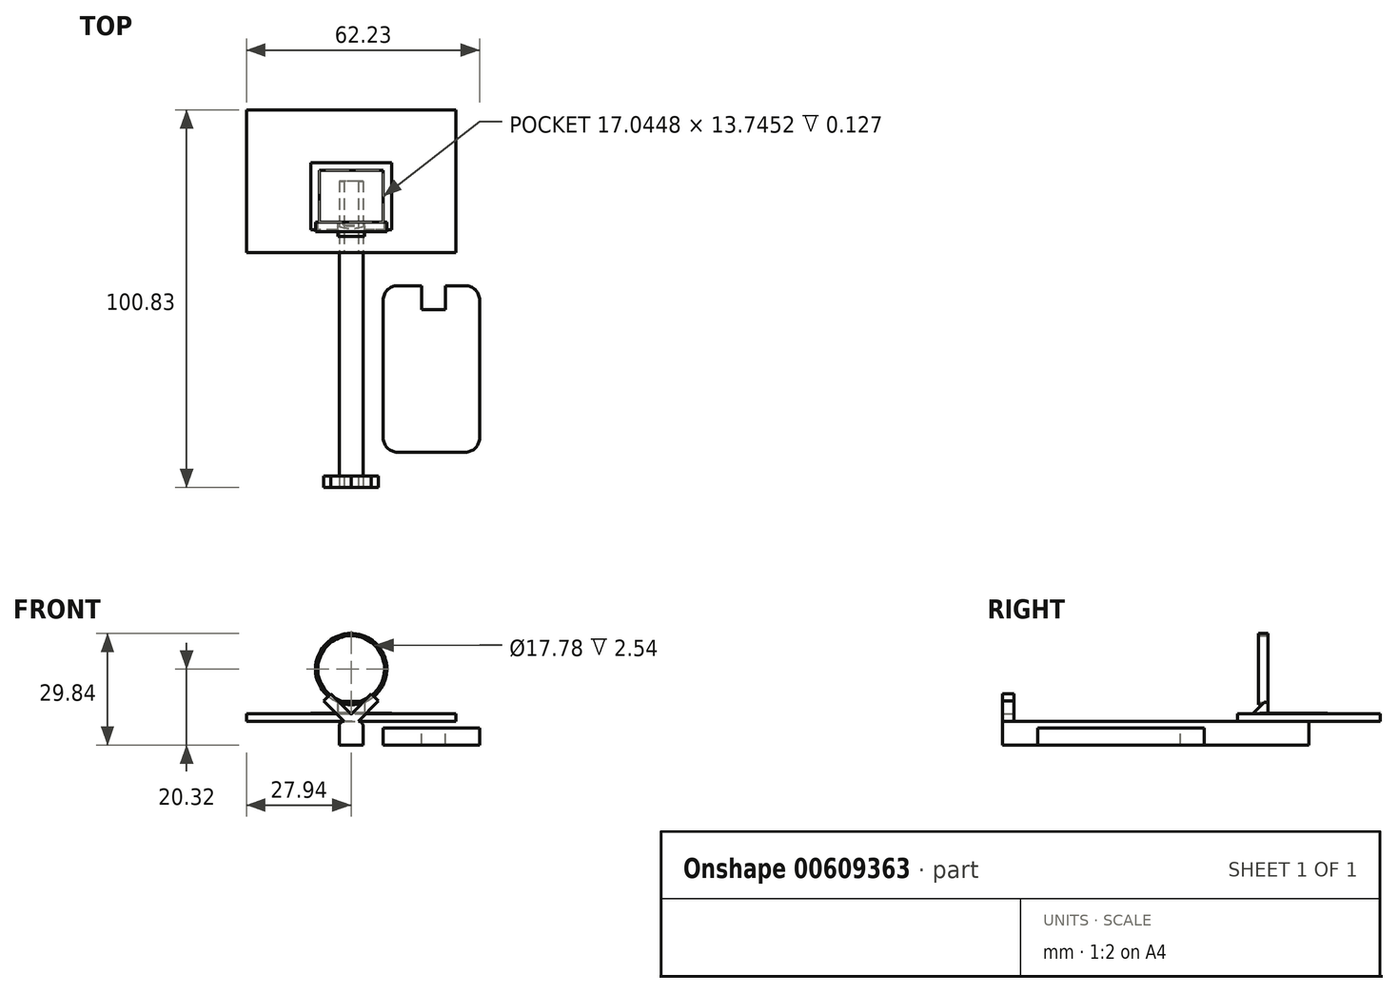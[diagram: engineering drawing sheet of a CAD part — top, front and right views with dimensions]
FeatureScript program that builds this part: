
annotation { "Feature Type Name" : "Feature", "Feature Type Description" : "" }
export const myFeature = defineFeature(function(context is Context, id is Id, definition is map)
    precondition{}
    {
        {
            var Q0;
            Q0=qCreatedBy(makeId("Top.planeOp"),FACE);
            var sketch = newSketch(context, id + "F0", { "sketchPlane" : qUnion([Q0])});
            skLineSegment(sketch, "E0.bottom", {"start": v(3.18, 3.17) * mm, "end": v(-3.18, 3.17) * mm});
            skLineSegment(sketch, "E0.top", {"start": v(3.18, -3.18) * mm, "end": v(-3.18, -3.18) * mm});
            skLineSegment(sketch, "E0.left", {"start": v(3.18, 3.17) * mm, "end": v(3.18, -3.18) * mm});
            skLineSegment(sketch, "E0.right", {"start": v(-3.18, 3.17) * mm, "end": v(-3.18, -3.18) * mm});
            skPoint(sketch, "E0.middle", {"position": v(0, 0) * mm});
            skSolve(sketch);
        }
        {
            var Q0;
            Q0 = qSketchRegion(id + "F0", true);
            extrude(context, id + "F1", {"entities" : qUnion([Q0]), "depth" : 81.8 * mm, "offsetDistance" : 25.4 * mm});
        }
        {
            var Q0;
            Q0=makeQuery(id+"F1.opExtrude","SWEPT_EDGE",EDGE,{"disambiguationData":[OSD([sQuery(id+"F0.wireOp",EDGE,"E0.top"),sQuery(id+"F0.wireOp",EDGE,"E0.right")])]});
            var Q1;
            {var subQ0=sQuery(id+"F0.wireOp",EDGE,"E0.top");var subQ1=sQuery(id+"F0.wireOp",EDGE,"E0.left");Q1=makeQuery(id+"FIJbQTMw3EpBJ4I_1.boolean.opBoolean","SPLIT",EDGE,{"disambiguationData":[topologyDisambiguationEdgeConnected([makeQuery(id+"F1.opExtrude","SWEPT_FACE",FACE,{"disambiguationData":[OSD([subQ1])]})])],"derivedFrom":makeQuery(id+"F1.opExtrude","SWEPT_EDGE",EDGE,{"disambiguationData":[OSD([subQ0,subQ1])]})});}
            fillet(context, id + "F2", {"entities" : qUnion([Q0, Q1]), "radius" : 1.27 * mm, "tangentPropagation" : true, "allowEdgeOverflow" : false});
        }
        {
            var Q0;
            Q0=makeQuery(id+"F1.opExtrude","SWEPT_FACE",FACE,{"disambiguationData":[OSD([sQuery(id+"F0.wireOp",EDGE,"E0.top")])]});
            var sketch = newSketch(context, id + "F3", { "sketchPlane" : qUnion([Q0])});
            skLineSegment(sketch, "E1.bottom", {"start": v(27.94, 62.74) * mm, "end": v(-27.94, 62.74) * mm});
            skLineSegment(sketch, "E1.top", {"start": v(27.94, 100.84) * mm, "end": v(-27.94, 100.84) * mm});
            skLineSegment(sketch, "E1.left", {"start": v(27.94, 62.74) * mm, "end": v(27.94, 100.84) * mm});
            skLineSegment(sketch, "E1.right", {"start": v(-27.94, 62.74) * mm, "end": v(-27.94, 100.84) * mm});
            skPoint(sketch, "E1.middle", {"position": v(0, 81.79) * mm});
            skSolve(sketch);
        }
        {
            var Q0;
            Q0 = qSketchRegion(id + "F3", true);
            extrude(context, id + "F4", {"entities" : qUnion([Q0]), "operationType" : NewBodyOperationType.ADD, "depth" : 2.03 * mm, "offsetDistance" : 25.4 * mm});
        }
        {
            var Q0;
            Q0=makeQuery(id+"F4.opExtrude","CAP_FACE",FACE,{"disambiguationData":[OSD([sQuery(id+"F3.wireOp",EDGE,"E1.bottom"),sQuery(id+"F3.wireOp",EDGE,"E1.top"),sQuery(id+"F3.wireOp",EDGE,"E1.left"),sQuery(id+"F3.wireOp",EDGE,"E1.right")])],"isStart":false});
            var sketch = newSketch(context, id + "F5", { "sketchPlane" : qUnion([Q0])});
            skLineSegment(sketch, "E2.bottom", {"start": v(10.81, 68.77) * mm, "end": v(-10.81, 68.77) * mm});
            skLineSegment(sketch, "E2.top", {"start": v(10.81, 86.76) * mm, "end": v(-10.81, 86.76) * mm});
            skLineSegment(sketch, "E2.left", {"start": v(10.81, 68.77) * mm, "end": v(10.81, 86.76) * mm});
            skLineSegment(sketch, "E2.right", {"start": v(-10.81, 68.77) * mm, "end": v(-10.81, 86.76) * mm});
            skPoint(sketch, "E2.middle", {"position": v(0, 77.76) * mm});
            skLineSegment(sketch, "E3.bottom", {"start": v(8.52, 84.64) * mm, "end": v(-8.52, 84.64) * mm});
            skLineSegment(sketch, "E3.top", {"start": v(8.52, 70.9) * mm, "end": v(-8.52, 70.9) * mm});
            skLineSegment(sketch, "E3.left", {"start": v(8.52, 84.64) * mm, "end": v(8.52, 70.9) * mm});
            skLineSegment(sketch, "E3.right", {"start": v(-8.52, 84.64) * mm, "end": v(-8.52, 70.9) * mm});
            skSolve(sketch);
        }
        {
            var Q0;
            Q0 = qSketchRegion(id + "F5", true);
            extrude(context, id + "F6", {"entities" : qUnion([Q0]), "operationType" : NewBodyOperationType.ADD, "depth" : 0.13 * mm, "offsetDistance" : 25.4 * mm});
        }
        {
            var Q0;
            Q0=makeQuery(id+"F6.boolean.opBoolean","SPLIT",FACE,{"disambiguationData":[TD([makeQuery(id+"F6.opExtrude","SWEPT_FACE",FACE,{"disambiguationData":[OSD([sQuery(id+"F5.wireOp",EDGE,"E3.bottom")])]})])],"derivedFrom":makeQuery(id+"F4.opExtrude","CAP_FACE",FACE,{"disambiguationData":[OSD([sQuery(id+"F3.wireOp",EDGE,"E1.bottom"),sQuery(id+"F3.wireOp",EDGE,"E1.top"),sQuery(id+"F3.wireOp",EDGE,"E1.left"),sQuery(id+"F3.wireOp",EDGE,"E1.right")])],"isStart":false})});
            var sketch = newSketch(context, id + "F7", { "sketchPlane" : qUnion([Q0])});
            skLineSegment(sketch, "E4.bottom", {"start": v(-3.54, 70.9) * mm, "end": v(3.54, 70.9) * mm});
            skLineSegment(sketch, "E4.top", {"start": v(-3.54, 67) * mm, "end": v(3.54, 67) * mm});
            skLineSegment(sketch, "E4.left", {"start": v(-3.54, 70.9) * mm, "end": v(-3.54, 67) * mm});
            skLineSegment(sketch, "E4.right", {"start": v(3.54, 70.9) * mm, "end": v(3.54, 67) * mm});
            skPoint(sketch, "E4.middle", {"position": v(0, 68.95) * mm});
            skPoint(sketch, "E4.middle.positionSnap0", {"position": v(0, 70.9) * mm});
            skPoint(sketch, "E4.centerSnap0", {"position": v(0, 70.9) * mm});
            skSolve(sketch);
        }
        {
            var Q0;
            Q0 = qSketchRegion(id + "F7", true);
            extrude(context, id + "F8", {"entities" : qUnion([Q0]), "operationType" : NewBodyOperationType.ADD, "depth" : 0.76 * mm, "offsetDistance" : 25.4 * mm});
        }
        {
            var Q0;
            Q0=makeQuery(id+"F8.opExtrude","CAP_FACE",FACE,{"disambiguationData":[OSD([sQuery(id+"F7.wireOp",EDGE,"E4.bottom"),sQuery(id+"F7.wireOp",EDGE,"E4.top"),sQuery(id+"F7.wireOp",EDGE,"E4.left"),sQuery(id+"F7.wireOp",EDGE,"E4.right")])],"isStart":false});
            var sketch = newSketch(context, id + "F9", { "sketchPlane" : qUnion([Q0])});
            skLineSegment(sketch, "E5.bottom", {"start": v(-3.54, 70.9) * mm, "end": v(3.54, 70.9) * mm});
            skLineSegment(sketch, "E5.top", {"start": v(-3.54, 67) * mm, "end": v(3.54, 67) * mm});
            skLineSegment(sketch, "E5.left", {"start": v(-3.54, 70.9) * mm, "end": v(-3.54, 67) * mm});
            skLineSegment(sketch, "E5.right", {"start": v(3.54, 70.9) * mm, "end": v(3.54, 67) * mm});
            skSolve(sketch);
        }
        {
            var Q0;
            Q0 = qSketchRegion(id + "F9", true);
            extrude(context, id + "F10", {"entities" : qUnion([Q0]), "operationType" : NewBodyOperationType.ADD, "depth" : 2.54 * mm, "offsetDistance" : 25.4 * mm});
        }
        {
            var Q0;
            Q0=makeQuery(id+"F10.opExtrude","CAP_EDGE",EDGE,{"disambiguationData":[OSD([sQuery(id+"F9.wireOp",EDGE,"E5.top")])],"isStart":false});
            chamfer(context, id + "F11", {"entities" : qUnion([Q0]), "width" : 3.05 * mm, "tangentPropagation" : true});
        }
        {
            var Q0;
            Q0=makeQuery(id+"F10.boolean.opBoolean","MERGE",FACE,{"derivedFrom":[makeQuery(id+"F8.boolean.opBoolean","MERGE",FACE,{"derivedFrom":[makeQuery(id+"F6.opExtrude","SWEPT_FACE",FACE,{"disambiguationData":[OSD([sQuery(id+"F5.wireOp",EDGE,"E3.top")])]}),makeQuery(id+"F8.opExtrude","SWEPT_FACE",FACE,{"disambiguationData":[OSD([sQuery(id+"F7.wireOp",EDGE,"E4.bottom")])]})]}),makeQuery(id+"F10.opExtrude","SWEPT_FACE",FACE,{"disambiguationData":[OSD([sQuery(id+"F9.wireOp",EDGE,"E5.bottom")])]})]});
            var sketch = newSketch(context, id + "F12", { "sketchPlane" : qUnion([Q0])});
            skCircle(sketch, "E6", {"center": v(0, -16.73) * mm, "radius": 9.53 * mm});
            skCircle(sketch, "E7", {"center": v(0, -16.73) * mm, "radius": 8.8 * mm});
            skSolve(sketch);
        }
        {
            var Q0;
            {var subQ1=sQuery(id+"F9.wireOp",EDGE,"E5.bottom");var subQ2=makeQuery(id+"F10.opExtrude","CAP_EDGE",EDGE,{"disambiguationData":[OSD([subQ1])],"isStart":false});var subQ5=sQuery(id+"F12.wireOp",EDGE,"E7");var subQ6=makeQuery(id+"F12.imprint","INTERSECT",VERTEX,{"disambiguationData":[OD(0.0)],"derivedFrom":[subQ2,subQ5]});Q0=makeQuery(id+"F12.imprint","IMPRINT",FACE,{"disambiguationData":[TD([[makeQuery(id+"F12.imprint","IMPRINT",EDGE,{"disambiguationData":[TD([[subQ6,-1.0]])],"derivedFrom":subQ5}),-1.0]])]});}
            extrude(context, id + "F13", {"entities" : qUnion([Q0]), "operationType" : NewBodyOperationType.ADD, "oppositeDirection" : true, "depth" : 0.76 * mm, "offsetDistance" : 25.4 * mm});
        }
        {
            var Q0;
            Q0=makeQuery(id+"F10.boolean.opBoolean","MERGE",FACE,{"derivedFrom":[makeQuery(id+"F8.boolean.opBoolean","MERGE",FACE,{"derivedFrom":[makeQuery(id+"F6.opExtrude","SWEPT_FACE",FACE,{"disambiguationData":[OSD([sQuery(id+"F5.wireOp",EDGE,"E3.top")])]}),makeQuery(id+"F8.opExtrude","SWEPT_FACE",FACE,{"disambiguationData":[OSD([sQuery(id+"F7.wireOp",EDGE,"E4.bottom")])]})]}),makeQuery(id+"F10.opExtrude","SWEPT_FACE",FACE,{"disambiguationData":[OSD([sQuery(id+"F9.wireOp",EDGE,"E5.bottom")])]})]});
            var sketch = newSketch(context, id + "F14", { "sketchPlane" : qUnion([Q0])});
            skCircle(sketch, "E8", {"center": v(0, -17.14) * mm, "radius": 9.53 * mm});
            skCircle(sketch, "E9", {"center": v(0, -17.14) * mm, "radius": 8.9 * mm});
            skPoint(sketch, "E10", {"position": v(0, -8.5) * mm});
            skSolve(sketch);
        }
        {
            var Q0;
            Q0 = qSketchRegion(id + "F14", true);
            extrude(context, id + "F15", {"entities" : qUnion([Q0]), "operationType" : NewBodyOperationType.ADD, "oppositeDirection" : true, "depth" : 2.54 * mm, "offsetDistance" : 25.4 * mm});
        }
        {
            var Q0;
            Q0=makeQuery(id+"F1.opExtrude","SWEPT_FACE",FACE,{"disambiguationData":[OSD([sQuery(id+"F0.wireOp",EDGE,"E0.top")])]});
            var sketch = newSketch(context, id + "F16", { "sketchPlane" : qUnion([Q0])});
            skLineSegment(sketch, "E11.bottom", {"start": v(-1.9, 3.08) * mm, "end": v(1.9, 3.08) * mm});
            skLineSegment(sketch, "E11.top", {"start": v(-1.9, 0) * mm, "end": v(1.9, 0) * mm});
            skLineSegment(sketch, "E11.left", {"start": v(-1.9, 3.08) * mm, "end": v(-1.9, 0) * mm});
            skLineSegment(sketch, "E11.right", {"start": v(1.9, 3.08) * mm, "end": v(1.9, 0) * mm});
            skSolve(sketch);
        }
        {
            var Q0;
            Q0 = qSketchRegion(id + "F16", true);
            extrude(context, id + "F17", {"entities" : qUnion([Q0]), "operationType" : NewBodyOperationType.ADD, "depth" : 2.54 * mm, "offsetDistance" : 25.4 * mm});
        }
        {
            var Q0;
            Q0=makeQuery(id+"F17.opExtrude","CAP_EDGE",EDGE,{"disambiguationData":[OSD([sQuery(id+"F16.wireOp",EDGE,"E11.right")])],"isStart":false});
            var Q1;
            Q1=makeQuery(id+"F17.opExtrude","CAP_EDGE",EDGE,{"disambiguationData":[OSD([sQuery(id+"F16.wireOp",EDGE,"E11.left")])],"isStart":false});
            chamfer(context, id + "F18", {"entities" : qUnion([Q0, Q1]), "width" : 2.54 * mm, "tangentPropagation" : true});
        }
        {
            var Q0;
            Q0=makeQuery(id+"F18.opChamfer","BLEND_FACE",FACE,{"disambiguationData":[OSD([sQuery(id+"F16.wireOp",EDGE,"E11.left")])]});
            extrude(context, id + "F19", {"entities" : qUnion([Q0]), "operationType" : NewBodyOperationType.ADD, "depth" : 7.62 * mm, "offsetDistance" : 25.4 * mm});
        }
        {
            var Q0;
            Q0=qCreatedBy(makeId("Right.planeOp"),FACE);
            var sketch = newSketch(context, id + "F20", { "sketchPlane" : qUnion([Q0])});
            skLineSegment(sketch, "E12.bottom", {"start": v(-176.52, 2.54) * mm, "end": v(-146.63, 2.54) * mm});
            skLineSegment(sketch, "E12.top", {"start": v(-176.52, 7.74) * mm, "end": v(-146.63, 7.74) * mm});
            skLineSegment(sketch, "E12.left", {"start": v(-176.52, 2.54) * mm, "end": v(-176.52, 7.74) * mm});
            skLineSegment(sketch, "E12.right", {"start": v(-146.63, 2.54) * mm, "end": v(-146.63, 7.74) * mm});
            skSolve(sketch);
        }
        {
            var Q0;
            {var subQ0=sQuery(id+"F16.wireOp",EDGE,"E11.right");Q0=makeQuery(id+"F19.boolean.opBoolean","MERGE",FACE,{"derivedFrom":[makeQuery(id+"F18.opChamfer","BLEND_FACE",FACE,{"disambiguationData":[OSD([subQ0])]}),makeQuery(id+"F19.opExtrude","SWEPT_FACE",FACE,{"disambiguationData":[OSD([sQuery(id+"F16.wireOp",EDGE,"E11.left"),subQ0])]})]});}
            var sketch = newSketch(context, id + "F21", { "sketchPlane" : qUnion([Q0])});
            skLineSegment(sketch, "E13.bottom", {"start": v(-3.6, 3.08) * mm, "end": v(-0.9, 3.08) * mm});
            skLineSegment(sketch, "E13.top", {"start": v(-3.6, 0) * mm, "end": v(-0.9, 0) * mm});
            skLineSegment(sketch, "E13.left", {"start": v(-3.6, 3.08) * mm, "end": v(-3.6, 0) * mm});
            skLineSegment(sketch, "E13.right", {"start": v(-0.9, 3.08) * mm, "end": v(-0.9, 0) * mm});
            skSolve(sketch);
        }
        {
            var Q0;
            Q0 = qSketchRegion(id + "F21", true);
            extrude(context, id + "F22", {"entities" : qUnion([Q0]), "operationType" : NewBodyOperationType.ADD, "depth" : 7.62 * mm, "offsetDistance" : 25.4 * mm});
        }
        {
            var Q0;
            Q0=makeQuery(id+"F20.imprint","IMPRINT",FACE,{"disambiguationData":[TD([[makeQuery(id+"F20.imprint","IMPRINT",EDGE,{"derivedFrom":sQuery(id+"F20.wireOp",EDGE,"E12.bottom")}),1.0]])]});
            var sketch = newSketch(context, id + "F23", { "sketchPlane" : qUnion([Q0])});
            skLineSegment(sketch, "E14.bottom", {"start": v(-34.39, 0) * mm, "end": v(-60.1, 0) * mm});
            skLineSegment(sketch, "E14.top", {"start": v(-34.39, 4.6) * mm, "end": v(-60.1, 4.6) * mm});
            skLineSegment(sketch, "E14.left", {"start": v(-34.39, 0) * mm, "end": v(-34.39, 4.6) * mm});
            skLineSegment(sketch, "E14.right", {"start": v(-60.1, 0) * mm, "end": v(-60.1, 4.6) * mm});
            skPoint(sketch, "E14.middle", {"position": v(-47.24, 2.3) * mm});
            skSolve(sketch);
        }
        {
            var Q0;
            Q0 = qSketchRegion(id + "F23", true);
            extrude(context, id + "F24", {"entities" : qUnion([Q0]), "operationType" : NewBodyOperationType.ADD, "depth" : 38.1 * mm, "offsetDistance" : 25.4 * mm});
        }
        {
            var Q0;
            {var subQ1=sQuery(id+"F23.wireOp",EDGE,"E14.top");var subQ6=sQuery(id+"F23.wireOp",EDGE,"E14.left");var subQ7=sQuery(id+"F23.wireOp",EDGE,"E14.bottom");Q0=makeQuery(id+"F24.boolean.opBoolean","SPLIT",FACE,{"disambiguationData":[TD([makeQuery(id+"F24.opExtrude","SWEPT_FACE",FACE,{"disambiguationData":[OSD([subQ6])]})])],"derivedFrom":makeQuery(id+"F24.opExtrude","CAP_FACE",FACE,{"disambiguationData":[OSD([subQ7,subQ1,subQ6,sQuery(id+"F23.wireOp",EDGE,"E14.right")])],"isStart":true})});}
            var Q1;
            {var subQ1=sQuery(id+"F23.wireOp",EDGE,"E14.top");var subQ6=sQuery(id+"F23.wireOp",EDGE,"E14.bottom");var subQ7=sQuery(id+"F23.wireOp",EDGE,"E14.right");Q1=makeQuery(id+"F24.boolean.opBoolean","SPLIT",FACE,{"disambiguationData":[TD([makeQuery(id+"F24.opExtrude","SWEPT_FACE",FACE,{"disambiguationData":[OSD([subQ7])]})])],"derivedFrom":makeQuery(id+"F24.opExtrude","CAP_FACE",FACE,{"disambiguationData":[OSD([subQ6,subQ1,sQuery(id+"F23.wireOp",EDGE,"E14.left"),subQ7])],"isStart":true})});}
            extrude(context, id + "F25", {"entities" : qUnion([Q0, Q1]), "operationType" : NewBodyOperationType.ADD, "depth" : 6.35 * mm, "offsetDistance" : 25.4 * mm});
        }
        {
            var Q0;
            Q0=makeQuery(id+"F24.opExtrude","CAP_EDGE",EDGE,{"disambiguationData":[OSD([sQuery(id+"F23.wireOp",EDGE,"E14.left")])],"isStart":false});
            var Q1;
            Q1=makeQuery(id+"F24.opExtrude","CAP_EDGE",EDGE,{"disambiguationData":[OSD([sQuery(id+"F23.wireOp",EDGE,"E14.right")])],"isStart":false});
            var Q2;
            Q2=makeQuery(id+"F25.opExtrude","CAP_EDGE",EDGE,{"disambiguationData":[OSD([sQuery(id+"F23.wireOp",EDGE,"E14.left")])],"isStart":false});
            var Q3;
            Q3=makeQuery(id+"F25.opExtrude","CAP_EDGE",EDGE,{"disambiguationData":[OSD([sQuery(id+"F23.wireOp",EDGE,"E14.right")])],"isStart":false});
            fillet(context, id + "F26", {"entities" : qUnion([Q0, Q1, Q2, Q3]), "radius" : 3.8 * mm, "tangentPropagation" : true, "allowEdgeOverflow" : false});
        }
        {
            var Q0;
            Q0=makeQuery(id+"F25.opExtrude","CAP_FACE",FACE,{"disambiguationData":[OSD([sQuery(id+"F23.wireOp",EDGE,"E14.bottom"),sQuery(id+"F23.wireOp",EDGE,"E14.top"),sQuery(id+"F23.wireOp",EDGE,"E14.left"),sQuery(id+"F23.wireOp",EDGE,"E14.right")])],"isStart":false});
            var sketch = newSketch(context, id + "F27", { "sketchPlane" : qUnion([Q0])});
            skLineSegment(sketch, "E15.bottom", {"start": v(49.84, 0) * mm, "end": v(43.49, 0) * mm});
            skLineSegment(sketch, "E15.top", {"start": v(49.84, 4.7) * mm, "end": v(43.49, 4.7) * mm});
            skLineSegment(sketch, "E15.left", {"start": v(49.84, 0) * mm, "end": v(49.84, 4.7) * mm});
            skLineSegment(sketch, "E15.right", {"start": v(43.49, 0) * mm, "end": v(43.49, 4.7) * mm});
            skPoint(sketch, "E15.middle", {"position": v(46.66, 2.35) * mm});
            skSolve(sketch);
        }
        {
            var Q0;
            Q0 = qSketchRegion(id + "F27", true);
            extrude(context, id + "F28", {"entities" : qUnion([Q0]), "operationType" : NewBodyOperationType.REMOVE, "oppositeDirection" : true, "depth" : 6.35 * mm, "offsetDistance" : 25.4 * mm});
        }
        {
            var Q0;
            Q0=makeQuery(id+"F1.opExtrude","SWEPT_BODY",BODY,{"disambiguationData":[OSD([sQuery(id+"F0.wireOp",EDGE,"E0.bottom"),sQuery(id+"F0.wireOp",EDGE,"E0.top"),sQuery(id+"F0.wireOp",EDGE,"E0.left"),sQuery(id+"F0.wireOp",EDGE,"E0.right")])]});
            var Q1;
            Q1=makeQuery(id+"F1.opExtrude","CAP_EDGE",EDGE,{"disambiguationData":[OSD([sQuery(id+"F0.wireOp",EDGE,"E0.bottom")])],"isStart":true});
            transform(context, id + "F29", {"entities" : qUnion([Q0]), "transformType" : TransformType.ROTATION, "transformAxis" : qUnion([Q1]), "angle" : 90 * degree, "makeCopy" : false});
        }
        {
            var Q0;
            Q0=makeQuery(id+"F24.opExtrude","SWEPT_BODY",BODY,{"disambiguationData":[OSD([sQuery(id+"F23.wireOp",EDGE,"E14.bottom"),sQuery(id+"F23.wireOp",EDGE,"E14.top"),sQuery(id+"F23.wireOp",EDGE,"E14.left"),sQuery(id+"F23.wireOp",EDGE,"E14.right")])]});
            var Q1;
            Q1=makeQuery(id+"F28.boolean.opBoolean","SPLIT",BODY,{"disambiguationData":[OD(0.0)],"derivedFrom":makeQuery(id+"F25.opExtrude","SWEPT_BODY",BODY,{"disambiguationData":[OSD([sQuery(id+"F23.wireOp",EDGE,"E14.bottom"),sQuery(id+"F23.wireOp",EDGE,"E14.top"),sQuery(id+"F23.wireOp",EDGE,"E14.left"),sQuery(id+"F23.wireOp",EDGE,"E14.right")])]})});
            var Q2;
            Q2=makeQuery(id+"F28.boolean.opBoolean","SPLIT",BODY,{"disambiguationData":[OD(1.0)],"derivedFrom":makeQuery(id+"F25.opExtrude","SWEPT_BODY",BODY,{"disambiguationData":[OSD([sQuery(id+"F23.wireOp",EDGE,"E14.bottom"),sQuery(id+"F23.wireOp",EDGE,"E14.top"),sQuery(id+"F23.wireOp",EDGE,"E14.left"),sQuery(id+"F23.wireOp",EDGE,"E14.right")])]})});
            var Q3;
            {var subQ0=sQuery(id+"F23.wireOp",EDGE,"E14.left");Q3=makeQuery(id+"F26.opFillet","BLEND_EDGE",EDGE,{"blendedFrom":[makeQuery(id+"F24.opExtrude","CAP_EDGE",EDGE,{"disambiguationData":[OSD([subQ0])],"isStart":false}),makeQuery(id+"F24.opExtrude","SWEPT_FACE",FACE,{"disambiguationData":[OSD([subQ0])]})],"blendedInto":[makeQuery(id+"F24.opExtrude","SWEPT_FACE",FACE,{"disambiguationData":[OSD([subQ0])]})]});}
            transform(context, id + "F30", {"entities" : qUnion([Q0, Q1, Q2]), "transformType" : TransformType.ROTATION, "transformAxis" : qUnion([Q3]), "angle" : 270 * degree, "makeCopy" : false});
        }
        {
            var Q0;
            Q0=makeQuery(id+"F1.opExtrude","SWEPT_BODY",BODY,{"disambiguationData":[OSD([sQuery(id+"F0.wireOp",EDGE,"E0.bottom"),sQuery(id+"F0.wireOp",EDGE,"E0.top"),sQuery(id+"F0.wireOp",EDGE,"E0.left"),sQuery(id+"F0.wireOp",EDGE,"E0.right")])]});
            var Q1;
            Q1=qCreatedBy(makeId("Front.planeOp"),FACE);
            transform(context, id + "F31", {"entities" : qUnion([Q0]), "transformType" : TransformType.TRANSLATION_DISTANCE, "transformDirection" : qUnion([Q1]), "distance" : 50.8 * mm, "makeCopy" : false});
        }
    });
